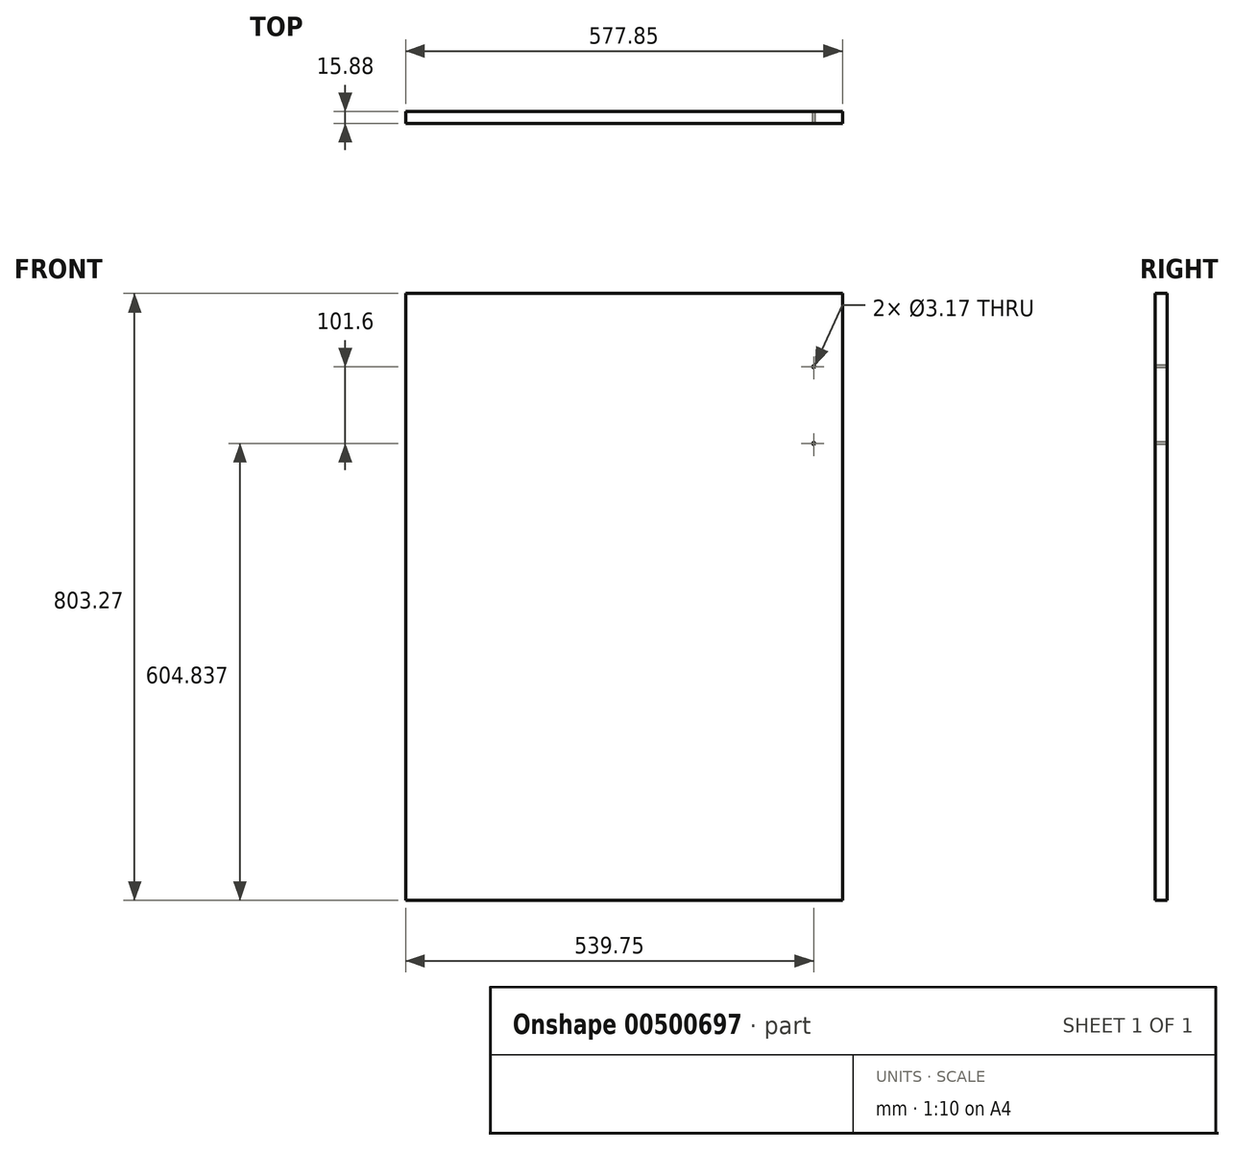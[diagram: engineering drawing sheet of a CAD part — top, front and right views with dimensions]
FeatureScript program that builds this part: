
annotation { "Feature Type Name" : "Feature", "Feature Type Description" : "" }
export const myFeature = defineFeature(function(context is Context, id is Id, definition is map)
    precondition{}
    {
        {
            var Q0;
            Q0=qCreatedBy(makeId("Front.planeOp"),FACE);
            var sketch = newSketch(context, id + "F0", { "sketchPlane" : qUnion([Q0])});
            skLineSegment(sketch, "E0.bottom", {"start": v(0, 0) * mm, "end": v(577.85, 0) * mm});
            skLineSegment(sketch, "E0.top", {"start": v(0, 803.28) * mm, "end": v(577.85, 803.28) * mm});
            skLineSegment(sketch, "E0.left", {"start": v(0, 0) * mm, "end": v(0, 803.27) * mm});
            skLineSegment(sketch, "E0.right", {"start": v(577.85, 0) * mm, "end": v(577.85, 803.28) * mm});
            skSolve(sketch);
        }
        {
            var Q0;
            Q0=makeQuery(id+"F0.imprint","IMPRINT",FACE,{"disambiguationData":[TD([[makeQuery(id+"F0.imprint","IMPRINT",EDGE,{"derivedFrom":sQuery(id+"F0.wireOp",EDGE,"E0.bottom")}),1.0]])]});
            extrude(context, id + "F1", {"entities" : qUnion([Q0]), "oppositeDirection" : true, "depth" : 15.88 * mm, "offsetDistance" : 25.4 * mm});
        }
        {
            var Q0;
            Q0=makeQuery(id+"F1.opExtrude","CAP_FACE",FACE,{"disambiguationData":[OSD([sQuery(id+"F0.wireOp",EDGE,"E0.bottom"),sQuery(id+"F0.wireOp",EDGE,"E0.top"),sQuery(id+"F0.wireOp",EDGE,"E0.left"),sQuery(id+"F0.wireOp",EDGE,"E0.right")])],"isStart":true});
            var sketch = newSketch(context, id + "F2", { "sketchPlane" : qUnion([Q0])});
            skLineSegment(sketch, "E1", {"start": v(577.85, 401.64) * mm, "end": v(-126.1, 401.64) * mm, "construction": true});
            skPoint(sketch, "E1.endSnap0", {"position": v(0, 401.64) * mm});
            skLineSegment(sketch, "E2.0", {"start": v(577.85, 452.44) * mm, "end": v(-126.1, 452.44) * mm});
            skLineSegment(sketch, "E3.0", {"start": v(577.85, 350.84) * mm, "end": v(-126.1, 350.84) * mm, "construction": true});
            skLineSegment(sketch, "E4", {"start": v(577.85, 452.44) * mm, "end": v(577.85, 350.84) * mm, "construction": true});
            skLineSegment(sketch, "E5.0", {"start": v(539.75, 452.44) * mm, "end": v(539.75, 350.84) * mm, "construction": true});
            skCircle(sketch, "E6", {"center": v(539.75, 452.44) * mm, "radius": 1.59 * mm, "construction": true});
            skCircle(sketch, "E7", {"center": v(539.75, 350.84) * mm, "radius": 1.59 * mm, "construction": true});
            skCircle(sketch, "E8.0.1.0", {"center": v(539.75, 706.44) * mm, "radius": 1.59 * mm});
            skCircle(sketch, "E8.0.1.1", {"center": v(539.75, 604.84) * mm, "radius": 1.59 * mm});
            skLineSegment(sketch, "E8.direction1", {"start": v(539.75, 452.44) * mm, "end": v(565.15, 452.44) * mm, "construction": true});
            skLineSegment(sketch, "E8.direction2", {"start": v(539.75, 452.44) * mm, "end": v(539.75, 706.44) * mm, "construction": true});
            skSolve(sketch);
        }
        {
            var Q0;
            Q0 = qSketchRegion(id + "F2", true);
            extrude(context, id + "F3", {"entities" : qUnion([Q0]), "operationType" : NewBodyOperationType.REMOVE, "endBound" : BoundingType.THROUGH_ALL, "oppositeDirection" : true, "depth" : 25.4 * mm, "offsetDistance" : 25.4 * mm});
        }
    });
